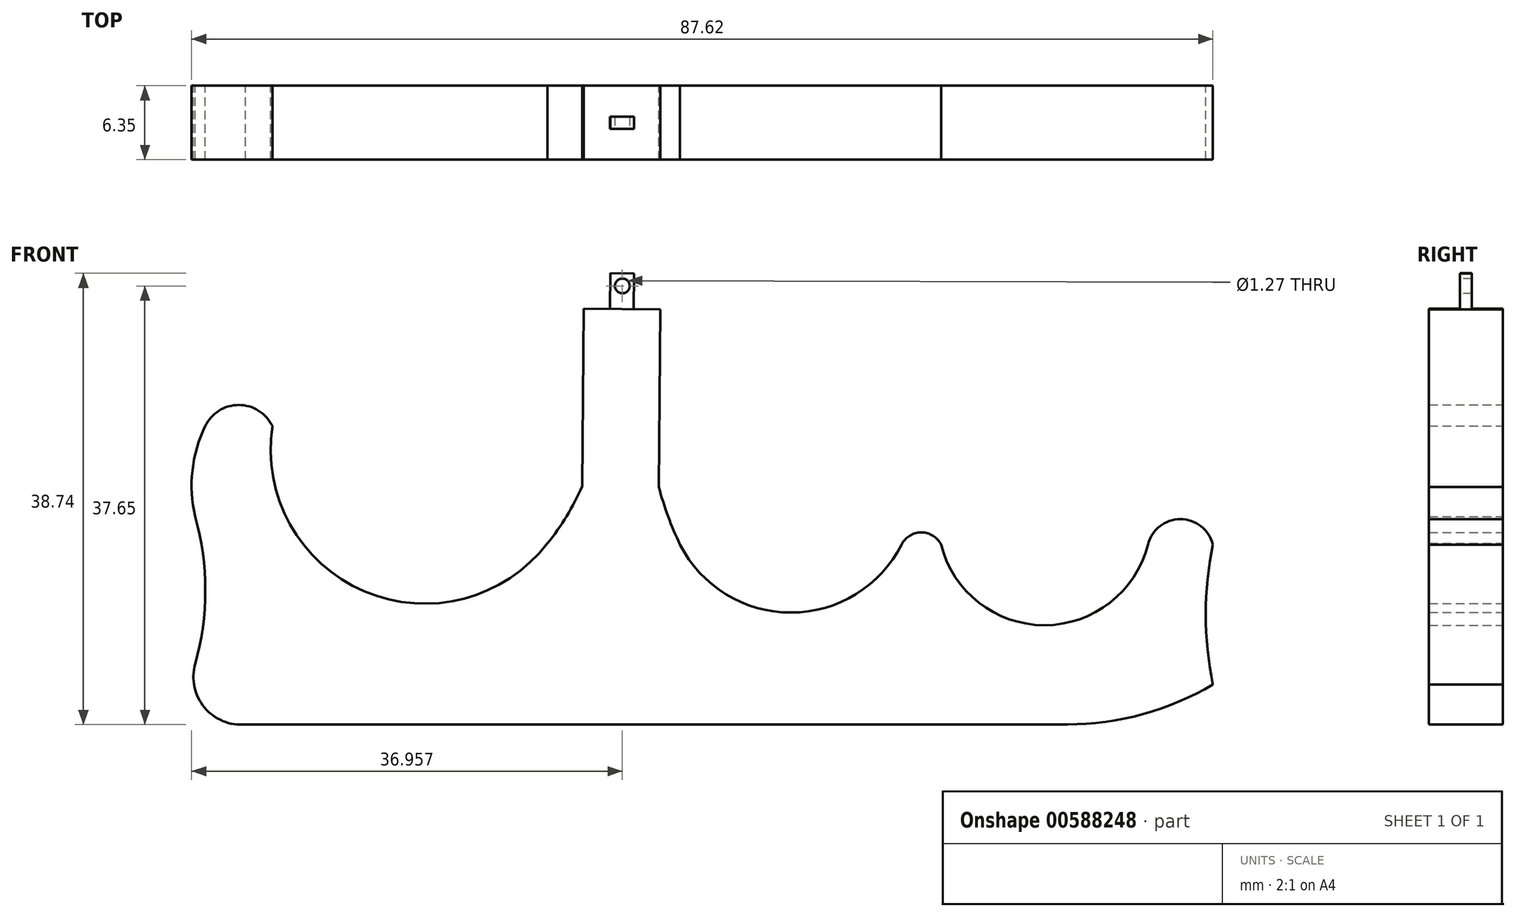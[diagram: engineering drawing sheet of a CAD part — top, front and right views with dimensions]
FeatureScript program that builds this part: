
annotation { "Feature Type Name" : "Feature", "Feature Type Description" : "" }
export const myFeature = defineFeature(function(context is Context, id is Id, definition is map)
    precondition{}
    {
        {
            var Q0;
            Q0=qCreatedBy(makeId("Front.planeOp"),FACE);
            var sketch = newSketch(context, id + "F0", { "sketchPlane" : qUnion([Q0])});
            skArc(sketch, "E0", {"start": v(-39.29, 17.7) * mm, "mid": v(-31.4, 3.51) * mm, "end": v(-15.69, 7.63) * mm});
            skLineSegment(sketch, "E1", {"start": v(-7.91, -7.91) * mm, "end": v(28.92, -7.91) * mm});
            skArc(sketch, "E2", {"start": v(-45.9, -2.73) * mm, "mid": v(-45.03, 3.6) * mm, "end": v(-45.9, 9.93) * mm});
            skLineSegment(sketch, "E3", {"start": v(-7.91, -7.91) * mm, "end": v(-41.59, -7.91) * mm});
            skArc(sketch, "E4", {"start": v(-45.9, -2.73) * mm, "mid": v(-45.1, -6.46) * mm, "end": v(-41.59, -7.91) * mm});
            skArc(sketch, "E5", {"start": v(41.4, 7.53) * mm, "mid": v(40.8, 1.52) * mm, "end": v(41.4, -4.48) * mm});
            skArc(sketch, "E6", {"start": v(28.92, -7.91) * mm, "mid": v(35.4, -7.04) * mm, "end": v(41.4, -4.48) * mm});
            skArc(sketch, "E7", {"start": v(-4.3, 7.53) * mm, "mid": v(5.2, 1.69) * mm, "end": v(14.7, 7.53) * mm});
            skArc(sketch, "E8", {"start": v(18.09, 7.53) * mm, "mid": v(26.96, 0.6) * mm, "end": v(35.84, 7.53) * mm});
            skArc(sketch, "E9", {"start": v(14.7, 7.53) * mm, "mid": v(16.4, 8.57) * mm, "end": v(18.09, 7.53) * mm});
            skPoint(sketch, "E10", {"position": v(-22.6, -2.16) * mm});
            skPoint(sketch, "E11", {"position": v(-9.12, 9) * mm});
            skPoint(sketch, "E12", {"position": v(-32.74, -4.74) * mm});
            skPoint(sketch, "E13", {"position": v(28.86, -3.5) * mm});
            skPoint(sketch, "E14", {"position": v(-42.4, 10) * mm});
            skPoint(sketch, "E15", {"position": v(-26.26, -6.24) * mm});
            skPoint(sketch, "E16", {"position": v(-11.63, -6.69) * mm});
            skArc(sketch, "E17", {"start": v(35.84, 7.53) * mm, "mid": v(38.62, 9.7) * mm, "end": v(41.4, 7.53) * mm});
            skArc(sketch, "E18", {"start": v(-45.04, 17.7) * mm, "mid": v(-46.14, 13.89) * mm, "end": v(-45.9, 9.93) * mm});
            skArc(sketch, "E19", {"start": v(-45.04, 17.7) * mm, "mid": v(-42.16, 19.5) * mm, "end": v(-39.29, 17.7) * mm});
            skPoint(sketch, "E20", {"position": v(-8.49, 36.03) * mm});
            skArc(sketch, "E21", {"start": v(-6.13, 12.46) * mm, "mid": v(-5.33, 9.95) * mm, "end": v(-4.3, 7.53) * mm});
            skArc(sketch, "E22", {"start": v(-15.69, 7.63) * mm, "mid": v(-14.03, 9.97) * mm, "end": v(-12.7, 12.51) * mm});
            skLineSegment(sketch, "E23", {"start": v(-12.7, 12.51) * mm, "end": v(-6.13, 12.46) * mm});
            skSolve(sketch);
        }
        {
            var Q0;
            Q0=makeQuery(id+"F0.imprint","IMPRINT",FACE,{"disambiguationData":[TD([[makeQuery(id+"F0.imprint","IMPRINT",EDGE,{"derivedFrom":sQuery(id+"F0.wireOp",EDGE,"E0")}),-1.0]])]});
            extrude(context, id + "F1", {"entities" : qUnion([Q0]), "depth" : 6.35 * mm, "offsetDistance" : 25.4 * mm});
        }
        {
            var Q0;
            Q0=makeQuery(id+"F1.opExtrude","SWEPT_FACE",FACE,{"disambiguationData":[OSD([sQuery(id+"F0.wireOp",EDGE,"E23")])]});
            var sketch = newSketch(context, id + "F2", { "sketchPlane" : qUnion([Q0])});
            skSolve(sketch);
        }
        {
            var Q0;
            {var subQ0=sQuery(id+"F2.wireOp",EDGE,"BiVFqbG0-JZYi-lWFu-ZR2w-ifGGmSjTSwOw");var subQ2=sQuery(id+"F0.wireOp",EDGE,"E23");var subQ4=makeQuery(id+"F1.opExtrude","CAP_EDGE",EDGE,{"disambiguationData":[OSD([subQ2])],"isStart":true});var subQ5=makeQuery(id+"F2.imprint","INTERSECT",VERTEX,{"disambiguationData":[OD(0.0)],"derivedFrom":[subQ4,subQ0]});Q0=makeQuery(id+"F2.imprint","IMPRINT",FACE,{"disambiguationData":[TD([[makeQuery(id+"F2.imprint","IMPRINT",EDGE,{"disambiguationData":[TD([[subQ5,1.0]])],"derivedFrom":subQ4}),-1.0]])]});}
            extrude(context, id + "F3", {"entities" : qUnion([Q0]), "operationType" : NewBodyOperationType.ADD, "depth" : 15.24 * mm, "offsetDistance" : 25.4 * mm});
        }
        {
            var Q0;
            Q0=makeQuery(id+"F3.opExtrude","CAP_FACE",FACE,{"disambiguationData":[OSD([sQuery(id+"F0.wireOp",EDGE,"E23"),sQuery(id+"F2.wireOp",EDGE,"XZbNkKlb-pVXw-lRhY-i0Ic-BphiM9e5lt6L"),sQuery(id+"F2.wireOp",EDGE,"BiVFqbG0-JZYi-lWFu-ZR2w-ifGGmSjTSwOw")])],"isStart":false});
            var sketch = newSketch(context, id + "F4", { "sketchPlane" : qUnion([Q0])});
            skPoint(sketch, "E24.endSnap0", {"position": v(-9.53, -3.18) * mm});
            skPoint(sketch, "E25.endSnap0", {"position": v(-9.02, -3.18) * mm});
            skLineSegment(sketch, "E26", {"start": v(-8.52, -2.67) * mm, "end": v(-8.52, -3.7) * mm});
            skLineSegment(sketch, "E27", {"start": v(-8.52, -3.7) * mm, "end": v(-10.55, -3.7) * mm});
            skLineSegment(sketch, "E28", {"start": v(-10.55, -3.7) * mm, "end": v(-10.55, -2.67) * mm});
            skLineSegment(sketch, "E29", {"start": v(-10.55, -2.67) * mm, "end": v(-8.52, -2.67) * mm});
            skSolve(sketch);
        }
        {
            var Q0;
            Q0=makeQuery(id+"F4.imprint","IMPRINT",FACE,{"disambiguationData":[TD([[makeQuery(id+"F4.imprint","IMPRINT",EDGE,{"derivedFrom":sQuery(id+"F4.wireOp",EDGE,"bBHshyRe-mEJX-lNAJ-BHsy-WEcGnLwDwfi5")}),-1.0]])]});
            var Q1;
            Q1=makeQuery(id+"F4.imprint","IMPRINT",FACE,{"disambiguationData":[TD([[makeQuery(id+"F4.imprint","IMPRINT",EDGE,{"derivedFrom":sQuery(id+"F4.wireOp",EDGE,"E26")}),-1.0]])]});
            extrude(context, id + "F5", {"entities" : qUnion([Q0, Q1]), "operationType" : NewBodyOperationType.ADD, "depth" : 3.07 * mm, "offsetDistance" : 25.4 * mm});
        }
        {
            var Q0;
            Q0=makeQuery(id+"F5.opExtrude","SWEPT_FACE",FACE,{"disambiguationData":[OSD([sQuery(id+"F4.wireOp",EDGE,"E27")])]});
            var sketch = newSketch(context, id + "F6", { "sketchPlane" : qUnion([Q0])});
            skPoint(sketch, "E30", {"position": v(-9.25, 29.25) * mm});
            skPoint(sketch, "E30.positionSnap0", {"position": v(-8.24, 29.25) * mm});
            skPoint(sketch, "E30.positionSnap1", {"position": v(-9.25, 30.8) * mm});
            skPoint(sketch, "E31", {"position": v(-9.25, 29.72) * mm});
            skSolve(sketch);
        }
        {
            var Q0;
            Q0=sQuery(id+"F6.wireOp",VERTEX,"E31");
            var Q1;
            Q1=makeQuery(id+"F1.opExtrude","SWEPT_BODY",BODY,{"disambiguationData":[OSD([sQuery(id+"F0.wireOp",EDGE,"E0"),sQuery(id+"F0.wireOp",EDGE,"E1"),sQuery(id+"F0.wireOp",EDGE,"E2"),sQuery(id+"F0.wireOp",EDGE,"E3"),sQuery(id+"F0.wireOp",EDGE,"E4"),sQuery(id+"F0.wireOp",EDGE,"E5"),sQuery(id+"F0.wireOp",EDGE,"E6"),sQuery(id+"F0.wireOp",EDGE,"E7"),sQuery(id+"F0.wireOp",EDGE,"E8"),sQuery(id+"F0.wireOp",EDGE,"E9"),sQuery(id+"F0.wireOp",EDGE,"E17"),sQuery(id+"F0.wireOp",EDGE,"E18"),sQuery(id+"F0.wireOp",EDGE,"E19"),sQuery(id+"F0.wireOp",EDGE,"E21"),sQuery(id+"F0.wireOp",EDGE,"E22"),sQuery(id+"F0.wireOp",EDGE,"E23")])]});
            hole(context, id + "F7", {"style" : HoleStyle.SIMPLE, "endStyle" : HoleEndStyle.THROUGH, "holeDiameter" : 1.27 * mm, "majorDiameter" : 6.35 * mm, "isTappedThrough" : true, "tappedDepth" : 12.7 * mm, "tapClearance" : 3, "locations" : qUnion([Q0]), "scope" : qUnion([Q1])});
        }
    });
